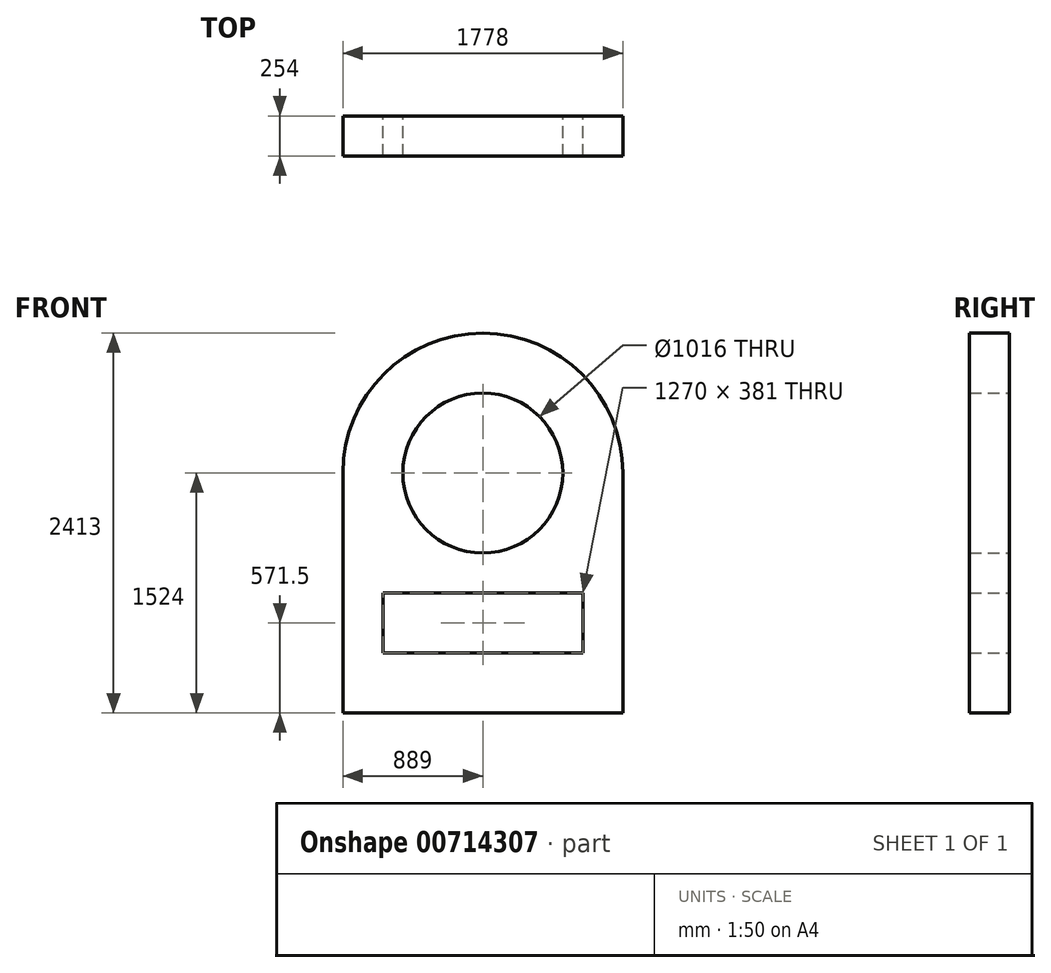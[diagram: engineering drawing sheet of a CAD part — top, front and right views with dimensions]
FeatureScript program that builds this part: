
annotation { "Feature Type Name" : "Feature", "Feature Type Description" : "" }
export const myFeature = defineFeature(function(context is Context, id is Id, definition is map)
    precondition{}
    {
        {
            var Q0;
            Q0=qCreatedBy(makeId("Front.planeOp"),FACE);
            var sketch = newSketch(context, id + "F0", { "sketchPlane" : qUnion([Q0])});
            skLineSegment(sketch, "E0", {"start": v(0, 0) * mm, "end": v(1778, 0) * mm});
            skLineSegment(sketch, "E1", {"start": v(0, 0) * mm, "end": v(0, 1524) * mm});
            skLineSegment(sketch, "E2", {"start": v(1778, 0) * mm, "end": v(1778, 1524) * mm});
            skArc(sketch, "E3", {"start": v(1778, 1524) * mm, "mid": v(889, 2413) * mm, "end": v(0, 1524) * mm});
            skCircle(sketch, "E4", {"center": v(889, 1524) * mm, "radius": 508 * mm});
            skLineSegment(sketch, "E5", {"start": v(254, 762) * mm, "end": v(254, 381) * mm});
            skLineSegment(sketch, "E6", {"start": v(254, 381) * mm, "end": v(1524, 381) * mm});
            skLineSegment(sketch, "E7", {"start": v(254, 762) * mm, "end": v(1524, 762) * mm});
            skLineSegment(sketch, "E8", {"start": v(1524, 762) * mm, "end": v(1524, 381) * mm});
            skSolve(sketch);
        }
        {
            var Q0;
            Q0 = qSketchRegion(id + "F0", true);
            extrude(context, id + "F1", {"entities" : qUnion([Q0]), "depth" : 254 * mm, "offsetDistance" : 25.4 * mm});
        }
    });
